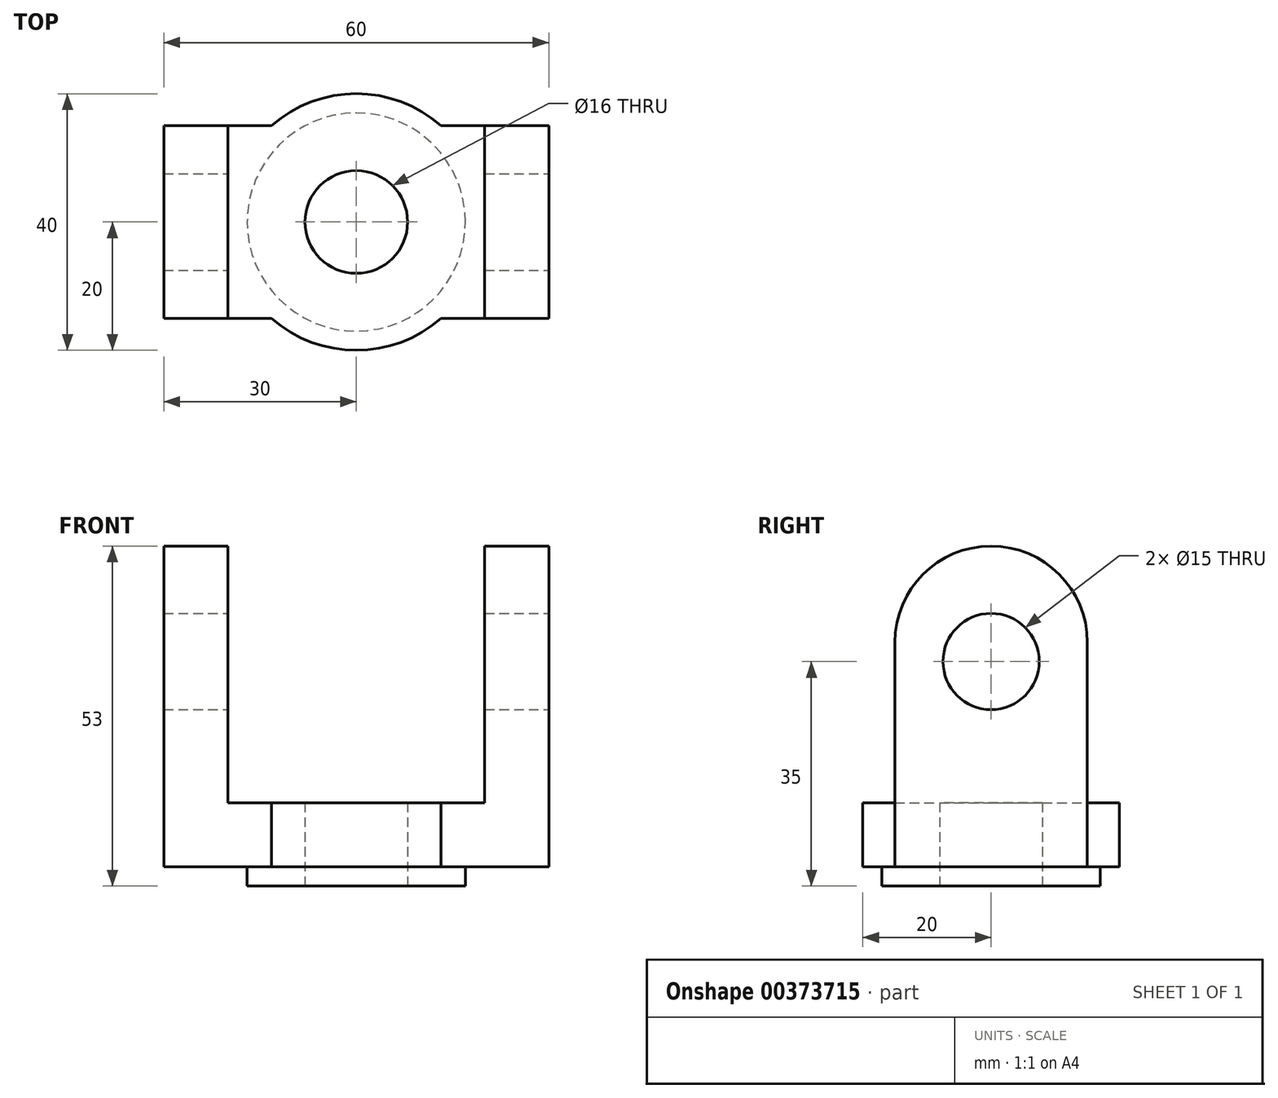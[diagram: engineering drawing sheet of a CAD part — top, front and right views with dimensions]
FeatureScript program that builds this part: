
annotation { "Feature Type Name" : "Feature", "Feature Type Description" : "" }
export const myFeature = defineFeature(function(context is Context, id is Id, definition is map)
    precondition{}
    {
        {
            var Q0;
            Q0=qCreatedBy(makeId("Top.planeOp"),FACE);
            var sketch = newSketch(context, id + "F0", { "sketchPlane" : qUnion([Q0])});
            skCircle(sketch, "E0", {"center": v(0, 0) * mm, "radius": 8 * mm});
            skCircle(sketch, "E1", {"center": v(0, 0) * mm, "radius": 20 * mm});
            skSolve(sketch);
        }
        {
            var Q0;
            Q0 = qSketchRegion(id + "F0", true);
            extrude(context, id + "F1", {"entities" : qUnion([Q0]), "depth" : 10 * mm});
        }
        {
            var Q0;
            Q0=qCreatedBy(makeId("Top.planeOp"),FACE);
            var sketch = newSketch(context, id + "F2", { "sketchPlane" : qUnion([Q0])});
            skCircle(sketch, "E2", {"center": v(0, 0) * mm, "radius": 17 * mm});
            skCircle(sketch, "E3", {"center": v(0, 0) * mm, "radius": 8 * mm});
            skSolve(sketch);
        }
        {
            var Q0;
            Q0 = qSketchRegion(id + "F2", true);
            extrude(context, id + "F3", {"entities" : qUnion([Q0]), "operationType" : NewBodyOperationType.ADD, "oppositeDirection" : true, "depth" : 3 * mm});
        }
        {
            var Q0;
            Q0=qCreatedBy(makeId("Front.planeOp"),FACE);
            var sketch = newSketch(context, id + "F4", { "sketchPlane" : qUnion([Q0])});
            skLineSegment(sketch, "E4", {"start": v(-30, 0) * mm, "end": v(-30, 50) * mm});
            skLineSegment(sketch, "E5", {"start": v(-30, 50) * mm, "end": v(-20, 50) * mm});
            skLineSegment(sketch, "E6", {"start": v(-20, 50) * mm, "end": v(-20, 10) * mm});
            skLineSegment(sketch, "E7", {"start": v(-20, 10) * mm, "end": v(20, 10) * mm});
            skLineSegment(sketch, "E8", {"start": v(20, 10) * mm, "end": v(20, 50) * mm});
            skLineSegment(sketch, "E9", {"start": v(20, 50) * mm, "end": v(30, 50) * mm});
            skLineSegment(sketch, "E10", {"start": v(30, 50) * mm, "end": v(30, 0) * mm});
            skLineSegment(sketch, "E11", {"start": v(30, 0) * mm, "end": v(-30, 0) * mm});
            skSolve(sketch);
        }
        {
            var Q0;
            Q0 = qSketchRegion(id + "F4", true);
            extrude(context, id + "F5", {"entities" : qUnion([Q0]), "operationType" : NewBodyOperationType.ADD, "endBound" : BoundingType.SYMMETRIC, "depth" : 30 * mm});
        }
        {
            var Q0;
            Q0=makeQuery(id+"F5.boolean.opBoolean","MERGE",FACE,{"derivedFrom":[makeQuery(id+"F1.opExtrude","CAP_FACE",FACE,{"disambiguationData":[OSD([sQuery(id+"F0.wireOp",EDGE,"E0"),sQuery(id+"F0.wireOp",EDGE,"E1")])],"isStart":false}),makeQuery(id+"F5.opExtrude","SWEPT_FACE",FACE,{"disambiguationData":[OSD([sQuery(id+"F4.wireOp",EDGE,"E7")])]})]});
            var sketch = newSketch(context, id + "F6", { "sketchPlane" : qUnion([Q0])});
            skCircle(sketch, "E12", {"center": v(0, 0) * mm, "radius": 8 * mm});
            skSolve(sketch);
        }
        {
            var Q0;
            Q0 = qSketchRegion(id + "F6", true);
            extrude(context, id + "F7", {"entities" : qUnion([Q0]), "operationType" : NewBodyOperationType.REMOVE, "oppositeDirection" : true, "depth" : 25 * mm});
        }
        {
            var Q0;
            Q0=qCreatedBy(makeId("Right.planeOp"),FACE);
            var sketch = newSketch(context, id + "F8", { "sketchPlane" : qUnion([Q0])});
            skCircle(sketch, "E13", {"center": v(0, 32) * mm, "radius": 7.5 * mm});
            skArc(sketch, "E14", {"start": v(15, 35) * mm, "mid": v(0, 50) * mm, "end": v(-15, 35) * mm});
            skLineSegment(sketch, "E15", {"start": v(-15, 35) * mm, "end": v(-15, 50) * mm});
            skLineSegment(sketch, "E16", {"start": v(-15, 50) * mm, "end": v(15, 50) * mm});
            skLineSegment(sketch, "E17", {"start": v(15, 50) * mm, "end": v(15, 35) * mm});
            skSolve(sketch);
        }
        {
            var Q0;
            Q0 = qSketchRegion(id + "F8", true);
            extrude(context, id + "F9", {"entities" : qUnion([Q0]), "operationType" : NewBodyOperationType.REMOVE, "endBound" : BoundingType.SYMMETRIC, "oppositeDirection" : true, "depth" : 60 * mm});
        }
    });
